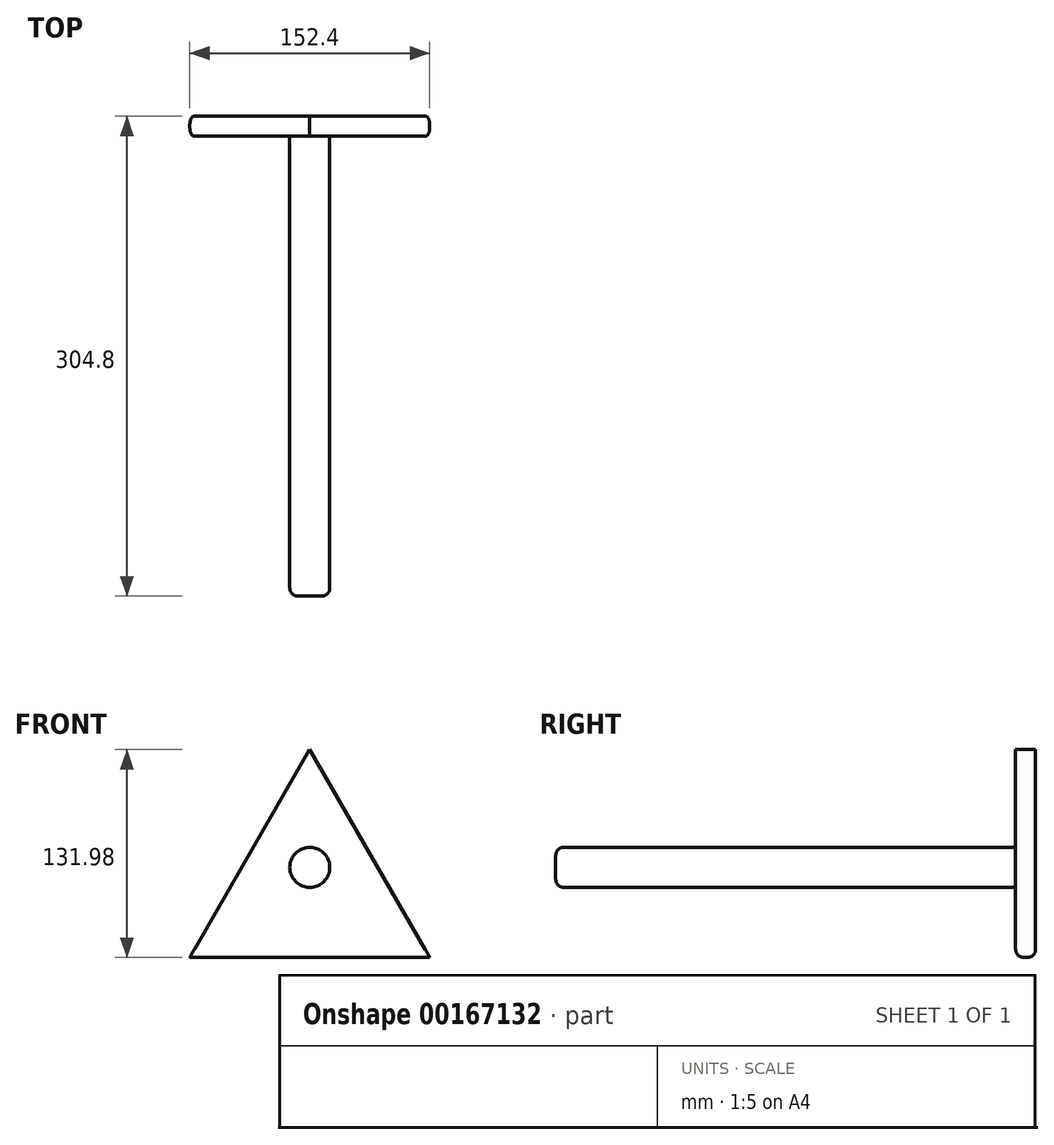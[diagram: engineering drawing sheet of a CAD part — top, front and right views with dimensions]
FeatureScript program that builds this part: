
annotation { "Feature Type Name" : "Feature", "Feature Type Description" : "" }
export const myFeature = defineFeature(function(context is Context, id is Id, definition is map)
    precondition{}
    {
        {
            var Q0;
            Q0=qCreatedBy(makeId("Front.planeOp"),FACE);
            var sketch = newSketch(context, id + "F0", { "sketchPlane" : qUnion([Q0])});
            skLineSegment(sketch, "E0", {"start": v(0, 74.82) * mm, "end": v(-76.2, -57.16) * mm});
            skLineSegment(sketch, "E1", {"start": v(-76.2, -57.16) * mm, "end": v(76.2, -57.16) * mm});
            skLineSegment(sketch, "E2", {"start": v(76.2, -57.16) * mm, "end": v(0, 74.82) * mm});
            skCircle(sketch, "E3", {"center": v(0, 0) * mm, "radius": 12.7 * mm});
            skSolve(sketch);
        }
        {
            var Q0;
            Q0 = qSketchRegion(id + "F0", true);
            extrude(context, id + "F1", {"entities" : qUnion([Q0]), "depth" : 12.7 * mm});
        }
        {
            var Q0;
            Q0=makeQuery(id+"F0.imprint","IMPRINT",FACE,{"disambiguationData":[TD([[makeQuery(id+"F0.imprint","IMPRINT",EDGE,{"derivedFrom":sQuery(id+"F0.wireOp",EDGE,"E3")}),1.0]])]});
            extrude(context, id + "F2", {"entities" : qUnion([Q0]), "operationType" : NewBodyOperationType.ADD, "depth" : 304.8 * mm});
        }
        {
            var Q0;
            Q0=makeQuery(id+"F2.opExtrude","CAP_EDGE",EDGE,{"disambiguationData":[OSD([sQuery(id+"F0.wireOp",EDGE,"E3")])],"isStart":false});
            fillet(context, id + "F3", {"entities" : qUnion([Q0]), "radius" : 5.08 * mm, "tangentPropagation" : true, "allowEdgeOverflow" : false});
        }
        {
            var Q0;
            Q0=makeQuery(id+"F1.opExtrude","CAP_EDGE",EDGE,{"disambiguationData":[OSD([sQuery(id+"F0.wireOp",EDGE,"E1")])],"isStart":false});
            fillet(context, id + "F4", {"entities" : qUnion([Q0]), "radius" : 5.08 * mm, "tangentPropagation" : true, "allowEdgeOverflow" : false});
        }
        {
            var Q0;
            Q0=makeQuery(id+"F1.opExtrude","CAP_EDGE",EDGE,{"disambiguationData":[OSD([sQuery(id+"F0.wireOp",EDGE,"E1")])],"isStart":true});
            fillet(context, id + "F5", {"entities" : qUnion([Q0]), "radius" : 5.08 * mm, "tangentPropagation" : true, "allowEdgeOverflow" : false});
        }
    });
